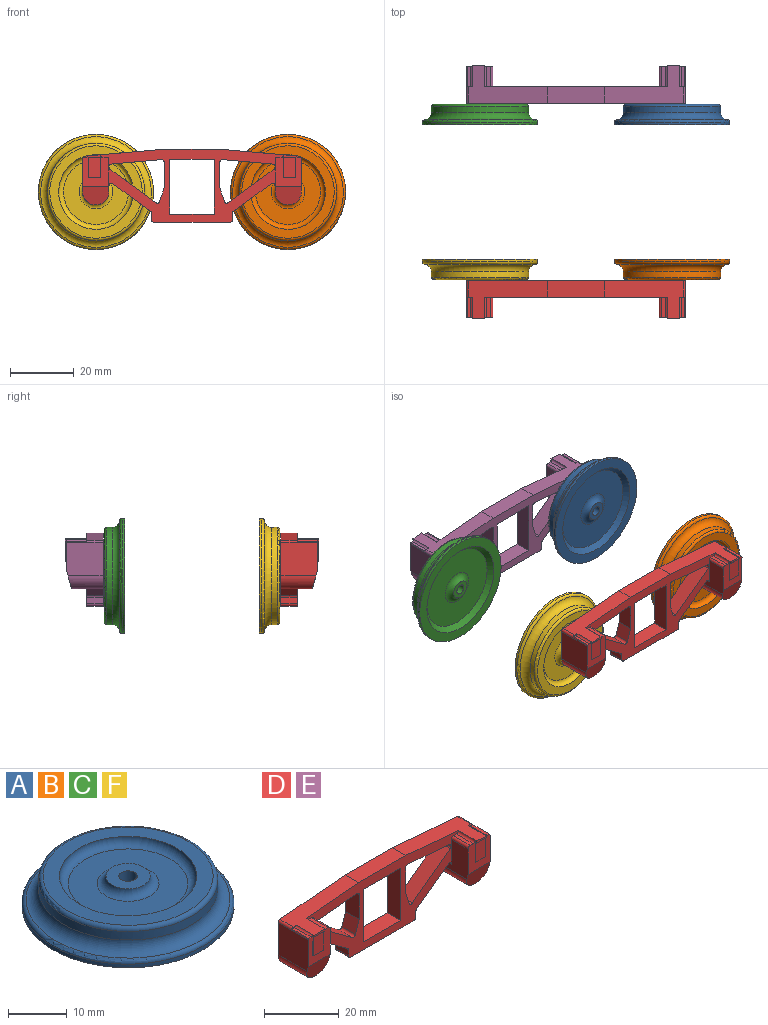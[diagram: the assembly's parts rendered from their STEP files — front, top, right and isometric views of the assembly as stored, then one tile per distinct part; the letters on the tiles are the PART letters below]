
ASSEMBLY  parts=6 mates=9
PART A: 16 faces, bbox 39x39x8.4 mm
  f0: plane 5.84x5.84mm, normal (0,0,-1), area 19.1mm2, adj f12,f15
  f1: plane 28.96x28.96mm, normal (0,0,1), area 229.6mm2, adj f6,f11
  f2: cylinder r=15.24mm len=30.48mm, axis (0,0,1), area 170.3mm2, adj f3,f6
  f3: torus R=17.53mm, axis (0,0,1), area 341.7mm2, adj f2,f7
  f4: cylinder r=18.03mm len=36.07mm, axis (0,0,1), area 87.5mm2, adj f5,f7
  f5: plane 36.07x36.07mm, normal (0,0,-1), area 328.1mm2, adj f4,f14
  f6: torus R=14.48mm, axis (0,0,-1), area 112.5mm2, adj f1,f2
  f7: torus R=17.27mm, axis (0,0,-1), area 126.6mm2, adj f3,f4
  f8: plane 20.32x20.32mm, normal (0,0,1), area 237mm2, adj f10,f11
  f9: plane 7.49x7.49mm, normal (0,0,1), area 36.4mm2, adj f10,f12
  f10: torus R=5.27mm, axis (0,0,1), area 64.7mm2, adj f8,f9
  f11: torus R=10.16mm, axis (0,0,1), area 167.4mm2, adj f1,f8
  f12: cylinder r=1.56mm len=6.35mm, axis (0,0,1), area 62.3mm2, adj f0,f9
  f13: plane 26.67x26.67mm, normal (0,0,-1), area 472.1mm2, adj f14,f15
  f14: cone r=13.33mm half-angle=45deg, axis (0,0,-1), area 190.9mm2, adj f5,f13
  f15: torus R=5.25mm, axis (0,0,-1), area 72.8mm2, adj f0,f13
PART B: same geometry as A
PART C: same geometry as A
PART D: 84 faces, bbox 68.6x12.3x22.9 mm
  f0: plane 9.93x8.26mm, normal (0,-1,0), area 51.5mm2, adj f3,f6,f9,f51,f56,f57,f60,f61
  f1: plane 9.93x8.26mm, normal (0,-1,0), area 51.5mm2, adj f2,f7,f10,f50,f53,f54,f58,f59
  f2: plane 11.43x10.14mm, normal (1,0,0), area 75.1mm2, adj f1,f11,f15,f35,f36,f46,f49,f50
  f3: plane 11.43x10.14mm, normal (-1,0,0), area 75.1mm2, adj f0,f12,f15,f35,f41,f42,f43,f51
  f4: plane 24.7x11.94mm, normal (0.09,0,1), area 152.2mm2, adj f6,f15,f31,f35,f55,f56,f61,f69
  f5: plane 24.7x11.94mm, normal (-0.09,0,1), area 152.2mm2, adj f7,f15,f31,f35,f52,f53,f59,f67
  f6: cylinder r=0.76mm len=11.43mm, axis (0,-1,0), area 8.6mm2, adj f0,f4,f9,f35,f55,f57
  f7: cylinder r=0.76mm len=11.43mm, axis (0,-1,0), area 8.6mm2, adj f1,f5,f10,f35,f52,f54
  f8: plane 9.88x0.13mm, normal (0,0,-1), area 1.3mm2, adj f12,f13,f35,f51
  f9: plane 11.43x10.48mm, normal (1,0,0), area 119.4mm2, adj f0,f6,f13,f35,f51
  f10: plane 11.43x10.48mm, normal (-1,0,0), area 119.4mm2, adj f1,f7,f14,f35,f50
  f11: cylinder r=4.06mm len=10.96mm, axis (0,1,0), area 65.6mm2, adj f2,f25,f35,f50
  f12: cylinder r=4.06mm len=10.96mm, axis (0,1,0), area 65.6mm2, adj f3,f8,f35,f51
  f13: cylinder r=4.06mm len=10.96mm, axis (0,-1,0), area 65.6mm2, adj f8,f9,f35,f51
  f14: cylinder r=4.06mm len=10.96mm, axis (0,-1,0), area 65.6mm2, adj f10,f25,f35,f50
  f15: plane 57.4x22.86mm, normal (0,-1,0), area 438.4mm2, adj f2,f3,f4,f5,f16,f17,f18,f19
  f16: plane 15.76x5.08mm, normal (0.09,0,-1), area 80.4mm2, adj f15,f35,f46,f47
  f17: plane 8.06x5.08mm, normal (-1,0,0), area 40.9mm2, adj f15,f18,f35,f47
  f18: plane 5.08x4.31mm, normal (-0.95,0,0.31), area 23mm2, adj f15,f17,f35,f48
  f19: plane 17.15x5.08mm, normal (1,0,0), area 87.1mm2, adj f15,f20,f32,f35
  f20: plane 13.97x5.08mm, normal (0,0,-1), area 71mm2, adj f15,f19,f21,f35
  f21: plane 17.15x5.08mm, normal (-1,0,0), area 87.1mm2, adj f15,f20,f32,f35
  f22: plane 15.76x5.08mm, normal (-0.09,0,-1), area 80.4mm2, adj f15,f35,f42,f45
  f23: plane 14.4x10.55mm, normal (-0.59,0,0.81), area 90.7mm2, adj f15,f35,f43,f44
  f24: plane 5.08x4.31mm, normal (0.95,0,0.31), area 23mm2, adj f15,f33,f35,f44
  f25: plane 9.88x0.13mm, normal (0,0,-1), area 1.3mm2, adj f11,f14,f35,f50
  f26: plane 11.81x8.66mm, normal (-0.59,0,-0.81), area 74.4mm2, adj f15,f35,f36,f37
  f27: plane 5.08x2.03mm, normal (-1,0,0), area 10.3mm2, adj f15,f35,f37,f38
  f28: plane 23.88x5.08mm, normal (0,0,-1), area 121.3mm2, adj f15,f35,f38,f39
  f29: plane 5.08x2.03mm, normal (1,0,0), area 10.3mm2, adj f15,f35,f39,f40
  f30: plane 11.81x8.66mm, normal (0.59,0,-0.81), area 74.4mm2, adj f15,f35,f40,f41
  f31: plane 17.78x5.08mm, normal (0,0,1), area 90.3mm2, adj f4,f5,f15,f35
  f32: plane 13.97x5.08mm, normal (0,0,1), area 71mm2, adj f15,f19,f21,f35
  f33: plane 8.06x5.08mm, normal (1,0,0), area 40.9mm2, adj f15,f24,f35,f45
  f34: plane 14.4x10.55mm, normal (0.59,0,0.81), area 90.7mm2, adj f15,f35,f48,f49
  f35: plane 68.58x22.86mm, normal (0,1,0), area 636.4mm2, adj f2,f3,f4,f5,f6,f7,f8,f9
  f36: cylinder r=0.76mm len=5.08mm, axis (0,1,0), area 8.5mm2, adj f2,f15,f26,f35
  f37: cylinder r=0.76mm len=5.08mm, axis (0,-1,0), area 3.6mm2, adj f15,f26,f27,f35
  f38: cylinder r=0.76mm len=5.08mm, axis (0,1,0), area 6.1mm2, adj f15,f27,f28,f35
  f39: cylinder r=0.76mm len=5.08mm, axis (0,-1,0), area 6.1mm2, adj f15,f28,f29,f35
  f40: cylinder r=0.76mm len=5.08mm, axis (0,-1,0), area 3.6mm2, adj f15,f29,f30,f35
  f41: cylinder r=0.76mm len=5.08mm, axis (0,1,0), area 8.5mm2, adj f3,f15,f30,f35
  f42: cylinder r=0.76mm len=5.08mm, axis (0,1,0), area 5.7mm2, adj f3,f15,f22,f35
  f43: cylinder r=0.76mm len=5.08mm, axis (0,-1,0), area 3.6mm2, adj f3,f15,f23,f35
  f44: cylinder r=0.76mm len=5.08mm, axis (0,1,0), area 7.3mm2, adj f15,f23,f24,f35
  f45: cylinder r=0.76mm len=5.08mm, axis (0,-1,0), area 6.4mm2, adj f15,f22,f33,f35
  f46: cylinder r=0.76mm len=5.08mm, axis (0,1,0), area 5.7mm2, adj f2,f15,f16,f35
  f47: cylinder r=0.76mm len=5.08mm, axis (0,-1,0), area 6.4mm2, adj f15,f16,f17,f35
  f48: cylinder r=0.76mm len=5.08mm, axis (0,1,0), area 7.3mm2, adj f15,f18,f34,f35
  f49: cylinder r=0.76mm len=5.08mm, axis (0,-1,0), area 3.6mm2, adj f2,f15,f34,f35
  f50: plane 8.26x5.8mm, normal (0,-0.97,-0.26), area 42.2mm2, adj f1,f2,f10,f11,f14,f25
  f51: plane 8.26x5.8mm, normal (0,-0.97,-0.26), area 42.2mm2, adj f0,f3,f8,f9,f12,f13
  f52: plane 1.65x0.43mm, normal (0,-1,0), area 0.5mm2, adj f5,f7,f54,f70
  f53: plane 6.78x0.51mm, normal (-1,0,0), area 1.8mm2, adj f1,f5,f62,f63,f66,f67
  f54: plane 6.35x0.96mm, normal (0,0,1), area 6.1mm2, adj f1,f7,f52,f70
  f55: plane 1.65x0.43mm, normal (0,-1,0), area 0.5mm2, adj f4,f6,f57,f73
  f56: plane 6.78x0.51mm, normal (1,0,0), area 1.8mm2, adj f0,f4,f64,f65,f68,f69
  f57: plane 6.35x0.96mm, normal (0,0,1), area 6.1mm2, adj f0,f6,f55,f73
  f58: plane 6.35x1.14mm, normal (0,0,1), area 7.3mm2, adj f1,f15,f71,f72
  f59: plane 7.11x0.51mm, normal (1,0,0), area 2mm2, adj f1,f5,f62,f63,f66,f67
  f60: plane 6.35x1.14mm, normal (0,0,1), area 7.3mm2, adj f0,f15,f74,f75
  f61: plane 7.11x0.51mm, normal (-1,0,0), area 2mm2, adj f0,f4,f64,f65,f68,f69
  f62: plane 3.81x0.25mm, normal (0,0,-1), area 1mm2, adj f1,f53,f59,f63
  f63: plane 6.35x3.81mm, normal (0,-1,0), area 24.2mm2, adj f53,f59,f62,f66
  f64: plane 3.81x0.25mm, normal (0,0,-1), area 1mm2, adj f0,f56,f61,f65
  f65: plane 6.35x3.81mm, normal (0,-1,0), area 24.2mm2, adj f56,f61,f64,f68
  f66: plane 3.81x0.25mm, normal (0,0,-1), area 1mm2, adj f53,f59,f63,f67
  f67: plane 3.81x0.76mm, normal (0,-1,0), area 2.3mm2, adj f5,f53,f59,f66
  f68: plane 3.81x0.25mm, normal (0,0,-1), area 1mm2, adj f56,f61,f65,f69
  f69: plane 3.81x0.76mm, normal (0,-1,0), area 2.3mm2, adj f4,f56,f61,f68
  f70: cylinder r=0.76mm len=6.35mm, axis (0,1,0), area 5.4mm2, adj f1,f5,f52,f54
  f71: cylinder r=0.76mm len=6.35mm, axis (0,-1,0), area 7.6mm2, adj f1,f2,f15,f58
  f72: cylinder r=0.76mm len=6.35mm, axis (0,1,0), area 7.6mm2, adj f1,f5,f15,f58
  f73: cylinder r=0.76mm len=6.35mm, axis (0,-1,0), area 5.4mm2, adj f0,f4,f55,f57
  f74: cylinder r=0.76mm len=6.35mm, axis (0,-1,0), area 7.6mm2, adj f0,f3,f15,f60
  f75: cylinder r=0.76mm len=6.35mm, axis (0,1,0), area 7.6mm2, adj f0,f4,f15,f60
  f76: cylinder r=2.54mm len=5.08mm, axis (0,-1,0), area 6.1mm2, adj f35,f77
  f77: plane 5.08x5.08mm, normal (0,1,0), area 12mm2, adj f76,f79
  f78: plane 3.25x3.25mm, normal (0,1,0), area 8.3mm2, adj f79
  f79: cylinder r=1.63mm len=3.56mm, axis (0,1,0), area 36.3mm2, adj f77,f78
  f80: cylinder r=2.54mm len=5.08mm, axis (0,-1,0), area 6.1mm2, adj f35,f81
  f81: plane 5.08x5.08mm, normal (0,1,0), area 12mm2, adj f80,f83
  f82: plane 3.25x3.25mm, normal (0,1,0), area 8.3mm2, adj f83
  f83: cylinder r=1.63mm len=3.56mm, axis (0,1,0), area 36.3mm2, adj f81,f82
PART E: same geometry as D
PART F: same geometry as A
PLACE A rot(axis=(-1,0,0),90deg) t=(-1.32,43.44,10.35)mm
PLACE B rot(axis=(1,0,0),90deg) t=(-1.32,1.17,10.35)mm
PLACE C rot(axis=(-1,0,0),90deg) t=(-61.52,43.44,10.35)mm
PLACE D rot(axis=(0,1,0),0deg) t=(-31.42,-5.56,12.31)mm
PLACE E rot(axis=(0,0,-1),180deg) t=(-31.42,50.17,12.31)mm
PLACE F rot(axis=(1,0,0),90deg) t=(-61.52,1.17,10.35)mm
MATE cylindrical E.f11 <-> A.f10  axis (0,-1,0) through (-1.32,51.56,10.35)mm
MATE cylindrical F.f14 <-> D.f11  axis (0,-1,0) through (-61.52,-2,10.35)mm
MATE cylindrical C.f14 <-> E.f12  axis (0,1,0) through (-61.52,46.61,10.35)mm
MATE fastened E.f12 <-> C.f3  axis (0,-1,0) through (-61.52,49.79,10.35)mm
MATE cylindrical D.f12 <-> B.f14  axis (0,1,0) through (-1.32,-6.96,10.35)mm
MATE fastened D.f12 <-> B.f10  axis (0,1,0) through (-1.32,-5.18,10.35)mm
MATE cylindrical F.f6 <-> C.f6  axis (0,-1,0) through (-61.52,-3.53,10.35)mm
MATE fastened F.f3 <-> D.f11  axis (0,-1,0) through (-61.52,-5.18,10.35)mm
MATE fastened A.f10 <-> E.f11  axis (0,1,0) through (-1.32,49.79,10.35)mm
